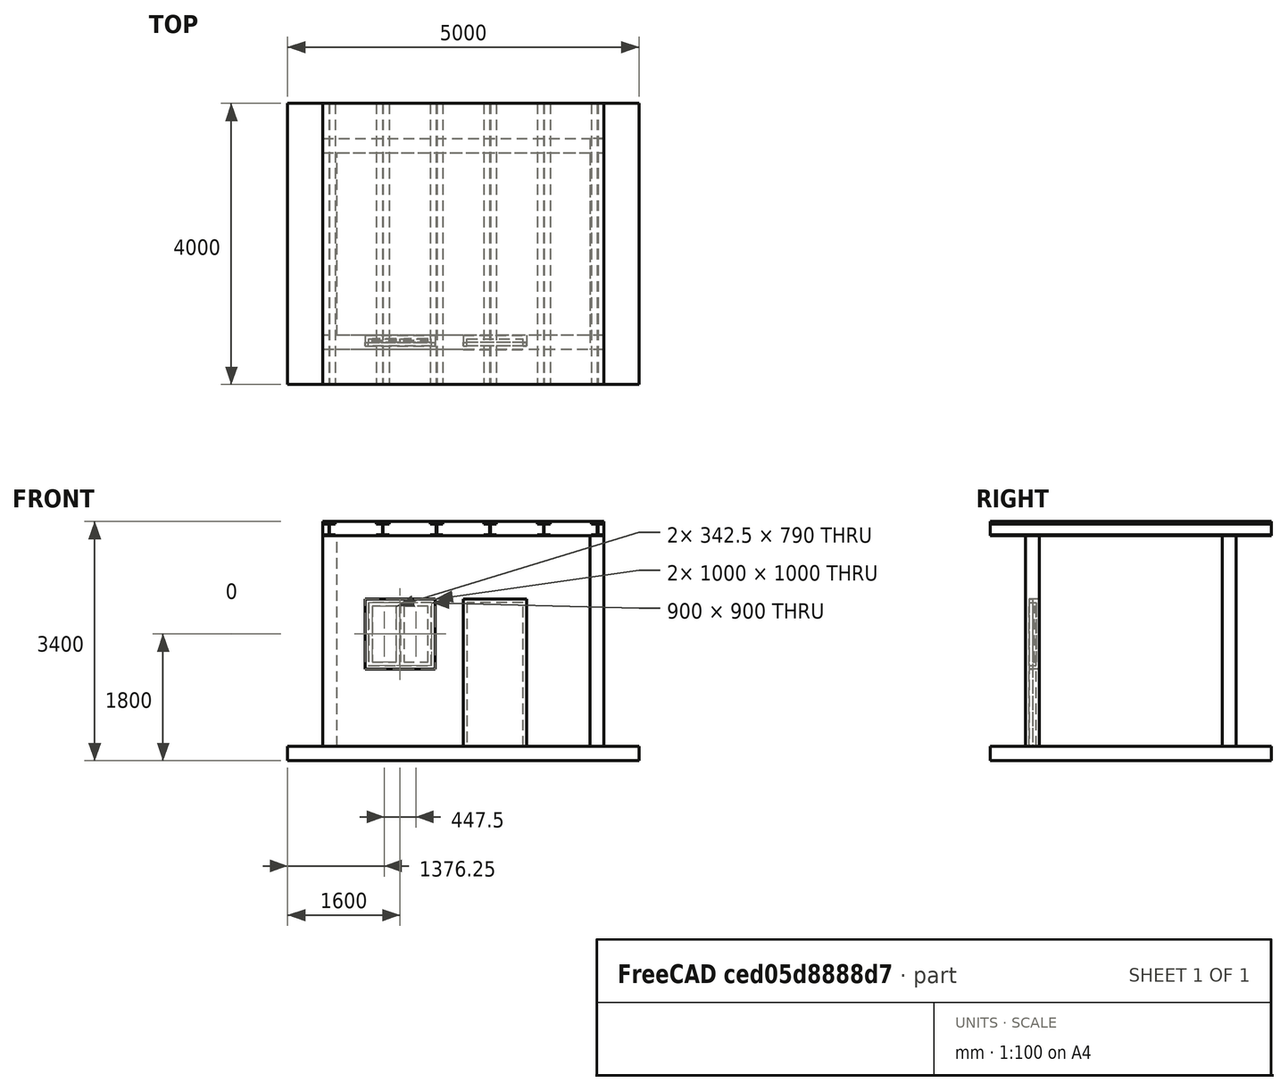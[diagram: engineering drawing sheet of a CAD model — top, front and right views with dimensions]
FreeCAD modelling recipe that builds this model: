
FCSTD DOCUMENT  (FreeCAD 0.17R7451 (Git))
Label: fem
License: All rights reserved
LicenseURL: http://en.wikipedia.org/wiki/All_rights_reserved
objects: Part::FeaturePython×12, Part::Part2DObjectPython×7, Sketcher::SketchObject×2, App::DocumentObjectGroupPython×2, Part::Feature×2, Part::MultiFuse×1, Fem::FemSolverObjectPython×1, Fem::FemMeshShapeNetgenObject×1, App::MaterialObjectPython×1, Fem::ConstraintFixed×1, Fem::ConstraintPressure×1, Fem::FemResultObject×1, Fem::FemAnalysisPython×1
note: 24 computed .brp shape members not serialized (recipe doc carries the construction recipe); baked Part::Feature solids carry a one-line shape summary decoded from their .brp

FEATURE [Part::Part2DObjectPython] Line  # Draft 2D object (typed FeaturePython)
  ChamferSize = 0
  Closed = false
  End = (0,3000,0)
  FilletRadius = 0
  Length = 3000
  MakeFace = false
  Points = (2) [(0,0,0),(0,3000,0)]
  Start = (0,0,0)
  Subdivisions = 0
FEATURE [Part::Part2DObjectPython] Line001  # Draft 2D object (typed FeaturePython)
  ChamferSize = 0
  Closed = false
  End = (4000,3000,0)
  FilletRadius = 0
  Length = 4000
  MakeFace = false
  Points = (2) [(0,3000,0),(4000,3000,0)]
  Start = (0,3000,0)
  Subdivisions = 0
FEATURE [Part::Part2DObjectPython] Line002  # Draft 2D object (typed FeaturePython)
  ChamferSize = 0
  Closed = false
  End = (4000,0,0)
  FilletRadius = 0
  Length = 3000
  MakeFace = false
  Points = (2) [(4000,3000,0),(4000,0,0)]
  Start = (4000,3000,0)
  Subdivisions = 0
FEATURE [Part::FeaturePython] Wall002  # WARN: FeaturePython — macro-defined, semantics opaque (R4)
  Align = 0
  Base = -> Line001
  Face = 0
  Height = 3000
  Length = 4000
  MoveWithHost = false
  Normal = (0,0,0)
  Role = 0
  Width = 200
FEATURE [Part::FeaturePython] Wall003  # WARN: FeaturePython — macro-defined, semantics opaque (R4)
  Align = 0
  Base = -> Line002
  Face = 0
  Height = 3000
  Length = 3000
  MoveWithHost = false
  Normal = (0,0,0)
  Role = 0
  Width = 200
FEATURE [Part::Part2DObjectPython] Line003  # Draft 2D object (typed FeaturePython)
  ChamferSize = 0
  Closed = false
  End = (0,0,0)
  FilletRadius = 0
  Length = 4000
  MakeFace = false
  Points = (2) [(4000,0,0),(0,0,0)]
  Start = (4000,0,0)
  Subdivisions = 0
FEATURE [Part::FeaturePython] Wall004  # WARN: FeaturePython — macro-defined, semantics opaque (R4)
  Align = 0
  Base = -> Line003
  Face = 0
  Height = 3000
  Length = 4000
  MoveWithHost = false
  Normal = (0,0,0)
  Role = 0
  Width = 200
FEATURE [Part::FeaturePython] Wall  # WARN: FeaturePython — macro-defined, semantics opaque (R4)
  Additions = -> [Wall004,Wall003,Wall002]
  Align = 0
  Base = -> Line
  Face = 0
  Height = 3000
  Length = 3000
  MoveWithHost = false
  Normal = (0,0,0)
  Role = 0
  Width = 200
FEATURE [Part::Part2DObjectPython] HEB180  # Draft 2D object (typed FeaturePython)
  FlangeThickness = 14
  Height = 180
  WebThickness = 8.5
  Width = 180
FEATURE [Part::FeaturePython] Structure  # WARN: FeaturePython — macro-defined, semantics opaque (R4)
  Base = -> HEB180
  Height = 4000
  Length = 0
  MoveWithHost = false
  Nodes = (2) [(1.65295e-14,-4.59631e-15,0),(1.65295e-14,-4.59631e-15,4000)]
  Normal = (0,0,0)
  Placement = pos=(90,3500,3090) rot=(1,0,0;1.5708rad)
  Profile = HEB180
  Role = 1
  Width = 200
FEATURE [Part::FeaturePython] Array  # Draft array (typed FeaturePython)
  Angle = 360
  ArrayType = 0
  Axis = (0,0,1)
  Base = -> Structure
  Center = (0,0,0)
  Fuse = false
  IntervalAxis = (0,0,0)
  IntervalX = (764,0,0)
  IntervalY = (0,1,0)
  IntervalZ = (0,0,0)
  NumberPolar = 1
  NumberX = 6
  NumberY = 1
  NumberZ = 1
FEATURE [Sketcher::SketchObject] Sketch
  MapMode = 5
  Placement = pos=(2000,0,0) rot=(1,0,0;1.5708rad)
  sketch-geometry (8):
    g0: LineSegment StartX=0 StartY=0 StartZ=0 EndX=900 EndY=0 EndZ=0
    g1: LineSegment StartX=900 StartY=0 StartZ=0 EndX=900 EndY=2100 EndZ=0
    g2: LineSegment StartX=900 StartY=2100 StartZ=0 EndX=0 EndY=2100 EndZ=0
    g3: LineSegment StartX=0 StartY=2100 StartZ=0 EndX=0 EndY=0 EndZ=0
    g4: LineSegment StartX=50 StartY=0 StartZ=0 EndX=850 EndY=0 EndZ=0
    g5: LineSegment StartX=850 StartY=0 StartZ=0 EndX=850 EndY=2050 EndZ=0
    g6: LineSegment StartX=850 StartY=2050 StartZ=0 EndX=50 EndY=2050 EndZ=0
    g7: LineSegment StartX=50 StartY=2050 StartZ=0 EndX=50 EndY=0 EndZ=0
  constraints (23):
    c: Coincident(g0,g1)
    c: Coincident(g1,g2)
    c: Coincident(g2,g3)
    c: Coincident(g3,g0)
    c: Horizontal(g0)
    c: Horizontal(g2)
    c: Vertical(g1)
    c: Vertical(g3)
    c: Coincident(g4,g5)
    c: Coincident(g5,g6)
    c: Coincident(g6,g7)
    c: Coincident(g7,g4)
    c: Horizontal(g4)
    c: Horizontal(g6)
    c: Vertical(g5)
    c: Vertical(g7)
    c: DistanceY(g1) = 2100
    c: DistanceX(g0) = 900
    c: DistanceY(g6,g2) = 50
    c: DistanceX(g2,g6) = 50
    c: DistanceX(g4,g0) = 50
    c: DistanceY(g0,g4) = 0
    c: Coincident(g0,g-1)
FEATURE [Part::FeaturePython] Window  # WARN: FeaturePython — macro-defined, semantics opaque (R4)
  Base = -> Sketch
  Height = 2100
  HoleDepth = 0
  MoveWithHost = true
  Normal = (0,1,0)
  Preset = 6
  Role = 1
  Width = 900
  WindowParts = OuterFrame | Frame | Wire0,Wire1 | 50.0 | 50.0 | Door | Solid panel | Wire1 | 50.0 | 100.0
FEATURE [Part::FeaturePython] Wall005  # WARN: FeaturePython — macro-defined, semantics opaque (R4)
  Align = 2
  Base = -> Wall
  Face = 0
  Height = 2000
  Length = 0
  MoveWithHost = false
  Normal = (0,0,0)
  Role = 0
  Subtractions = -> [Window]
  Width = 200
FEATURE [Sketcher::SketchObject] Sketch001
  MapMode = 5
  Placement = pos=(600,0,1100) rot=(1,0,0;1.5708rad)
  sketch-geometry (24):
    g0: LineSegment StartX=0 StartY=0 StartZ=0 EndX=1000 EndY=0 EndZ=0
    g1: LineSegment StartX=1000 StartY=0 StartZ=0 EndX=1000 EndY=1000 EndZ=0
    g2: LineSegment StartX=1000 StartY=1000 StartZ=0 EndX=0 EndY=1000 EndZ=0
    g3: LineSegment StartX=0 StartY=1000 StartZ=0 EndX=0 EndY=0 EndZ=0
    g4: LineSegment StartX=50 StartY=50 StartZ=0 EndX=950 EndY=50 EndZ=0
    g5: LineSegment StartX=950 StartY=50 StartZ=0 EndX=950 EndY=950 EndZ=0
    g6: LineSegment StartX=950 StartY=950 StartZ=0 EndX=50 EndY=950 EndZ=0
    g7: LineSegment StartX=50 StartY=950 StartZ=0 EndX=50 EndY=50 EndZ=0
    g8: LineSegment StartX=55 StartY=55 StartZ=0 EndX=497.5 EndY=55 EndZ=0
    g9: LineSegment StartX=497.5 StartY=55 StartZ=0 EndX=497.5 EndY=945 EndZ=0
    g10: LineSegment StartX=497.5 StartY=945 StartZ=0 EndX=55 EndY=945 EndZ=0
    g11: LineSegment StartX=55 StartY=945 StartZ=0 EndX=55 EndY=55 EndZ=0
    g12: LineSegment StartX=105 StartY=105 StartZ=0 EndX=447.5 EndY=105 EndZ=0
    g13: LineSegment StartX=447.5 StartY=105 StartZ=0 EndX=447.5 EndY=895 EndZ=0
    g14: LineSegment StartX=447.5 StartY=895 StartZ=0 EndX=105 EndY=895 EndZ=0
    g15: LineSegment StartX=105 StartY=895 StartZ=0 EndX=105 EndY=105 EndZ=0
    g16: LineSegment StartX=502.5 StartY=55 StartZ=0 EndX=945 EndY=55 EndZ=0
    g17: LineSegment StartX=945 StartY=55 StartZ=0 EndX=945 EndY=945 EndZ=0
    g18: LineSegment StartX=945 StartY=945 StartZ=0 EndX=502.5 EndY=945 EndZ=0
    g19: LineSegment StartX=502.5 StartY=945 StartZ=0 EndX=502.5 EndY=55 EndZ=0
    g20: LineSegment StartX=552.5 StartY=105 StartZ=0 EndX=895 EndY=105 EndZ=0
    g21: LineSegment StartX=895 StartY=105 StartZ=0 EndX=895 EndY=895 EndZ=0
    g22: LineSegment StartX=895 StartY=895 StartZ=0 EndX=552.5 EndY=895 EndZ=0
    g23: LineSegment StartX=552.5 StartY=895 StartZ=0 EndX=552.5 EndY=105 EndZ=0
  constraints (71):
    c: Coincident(g0,g1)
    c: Coincident(g1,g2)
    c: Coincident(g2,g3)
    c: Coincident(g3,g0)
    c: Horizontal(g0)
    c: Horizontal(g2)
    c: Vertical(g1)
    c: Vertical(g3)
    c: Coincident(g4,g5)
    c: Coincident(g5,g6)
    c: Coincident(g6,g7)
    c: Coincident(g7,g4)
    c: Horizontal(g4)
    c: Horizontal(g6)
    c: Vertical(g5)
    c: Vertical(g7)
    c: DistanceY(g1) = 1000
    c: DistanceX(g0) = 1000
    c: DistanceY(g6,g2) = 50
    c: DistanceX(g2,g6) = 50
    c: DistanceX(g4,g0) = 50
    c: DistanceY(g0,g4) = 50
    c: Coincident(g0,g-1)
    c: Coincident(g8,g9)
    c: Coincident(g9,g10)
    c: Coincident(g10,g11)
    c: Coincident(g11,g8)
    c: Horizontal(g8)
    c: Horizontal(g10)
    c: Vertical(g9)
    c: Vertical(g11)
    c: Coincident(g12,g13)
    c: Coincident(g13,g14)
    c: Coincident(g14,g15)
    c: Coincident(g15,g12)
    c: Horizontal(g12)
    c: Horizontal(g14)
    c: Vertical(g13)
    c: Vertical(g15)
    c: Coincident(g16,g17)
    c: Coincident(g17,g18)
    c: Coincident(g18,g19)
    c: Coincident(g19,g16)
    c: Horizontal(g16)
    c: Horizontal(g18)
    c: Vertical(g17)
    c: Vertical(g19)
    c: Coincident(g20,g21)
    c: Coincident(g21,g22)
    c: Coincident(g22,g23)
    c: Coincident(g23,g20)
    c: Horizontal(g20)
    c: Horizontal(g22)
    c: Vertical(g21)
    c: Vertical(g23)
    c: DistanceY(g8,g12) = 50
    c: DistanceX(g8,g12) = 50
    c: DistanceX(g21,g17) = 50
    c: DistanceY(g21,g17) = 50
    c: DistanceX(g16,g20) = 50
    c: DistanceX(g14,g10) = 50
    c: Equal(g22,g14)
    c: DistanceY(g8,g16) = 0
    c: DistanceY(g10,g18) = 0
    c: DistanceX(g4,g8) = 5
    c: DistanceY(g4,g8) = 5
    c: DistanceX(g6,g18) = -5
    c: DistanceY(g6,g18) = -5
    c: DistanceX(g9,g19) = 5
    c: PointOnObject(g13,g22)
    c: PointOnObject(g20,g12)
FEATURE [Part::FeaturePython] Window001  # WARN: FeaturePython — macro-defined, semantics opaque (R4)
  Base = -> Sketch001
  Height = 1000
  HoleDepth = 0
  MoveWithHost = true
  Normal = (0,1,0)
  Preset = 3
  Role = 0
  Width = 1000
  WindowParts = OuterFrame | Frame | Wire0,Wire1 | 50.0 | 50.0 | LeftFrame | Frame | Wire2,Wire3 | 50.0 | 100.0 | LeftGlass | Glass panel | Wire3 | 5.0 | 125.0 | RightFrame | Frame | Wire4,Wire5 | 50.0 | 100.0 | RightGlass | Glass panel | Wire5 | 5.0 | 125.0
FEATURE [Part::FeaturePython] Wall006  # WARN: FeaturePython — macro-defined, semantics opaque (R4)
  Align = 2
  Base = -> Wall005
  Face = 0
  Height = 2000
  Length = 0
  MoveWithHost = false
  Normal = (0,0,0)
  Role = 0
  Subtractions = -> [Window001]
  Width = 200
FEATURE [Part::Part2DObjectPython] Rectangle  # Draft 2D object (typed FeaturePython)
  ChamferSize = 0
  Columns = 1
  FilletRadius = 0
  Height = -4000
  Length = -4000
  MakeFace = true
  Placement = pos=(0,-500,3000) rot=(0,0,1;3.14159rad)
  Rows = 1
FEATURE [Part::FeaturePython] Structure001  # WARN: FeaturePython — macro-defined, semantics opaque (R4)
  Base = -> Rectangle
  Height = 200
  Length = 0
  MoveWithHost = false
  Nodes = (2) [(2000,1500,3000),(2000,1500,3200)]
  Normal = (0,0,1)
  Role = 1
  Width = 200
FEATURE [Part::Part2DObjectPython] Rectangle001  # Draft 2D object (typed FeaturePython)
  ChamferSize = 0
  Columns = 1
  FilletRadius = 0
  Height = -4000
  Length = 5000
  MakeFace = true
  Placement = pos=(-500,3500,0) rot=(0,0,1;0rad)
  Rows = 1
FEATURE [Part::FeaturePython] Structure002  # WARN: FeaturePython — macro-defined, semantics opaque (R4)
  Base = -> Rectangle001
  Height = 200
  Length = 0
  MoveWithHost = false
  Nodes = (2) [(2000,1500,0),(2000,1500,-200)]
  Normal = (0,0,-1)
  Role = 1
  Width = 200
FEATURE [App::DocumentObjectGroupPython] Floor  # scripted group (container) (typed FeaturePython)
  Group = -> [Array,Wall006,Structure001,Structure002]
  Height = 0
FEATURE [App::DocumentObjectGroupPython] Building  # scripted group (container) (typed FeaturePython)
  BuildingType = 0
  Group = -> [Floor]
  Height = 0
FEATURE [Part::Feature] Wall006001  label="Wall007"
  shape: bbox 4000 x 3000 x 3000 mm, 17 faces (baked)
FEATURE [Part::Feature] Structure001001  label="Structure003"
  shape: bbox 4000 x 4000 x 200 mm, 6 faces (baked)
FEATURE [Part::MultiFuse] Fusion
  Shapes = -> [Wall006001,Structure001001]
FEATURE [Fem::FemSolverObjectPython] CalculiX  # FEM object (typed FeaturePython)
  AnalysisType = 0
  EigenmodeHighLimit = 1000000
  EigenmodeLowLimit = 0
  NumberOfEigenmodes = 10
  SolverType = FemSolverCalculix
FEATURE [Fem::FemMeshShapeNetgenObject] Fusion_Mesh
  Fineness = 2
  GrowthRate = 0.3
  MaxSize = 1000
  NbSegsPerEdge = 1
  NbSegsPerRadius = 2
  Optimize = true
  SecondOrder = true
  Shape = -> Fusion
FEATURE [App::MaterialObjectPython] MechanicalMaterial  # material (typed FeaturePython)
  Material = CompressiveStrength=25 MPa,Density=2400 kg/m^3,Description=A standard C-25 construction concrete,Father=Aggregate,Name=Concrete,PoissonRatio=0.17,+3 more (map truncated)
FEATURE [Fem::ConstraintFixed] FemConstraintFixed
  NormalDirection = (0,0,-1)
  Normals = (24) [(0,0,-1),(0,0,-1),(0,0,-1),(0,0,-1),(0,0,-1),(0,0,-1),(0,0,-1),(0,0,-1),(0,0,-1),(0,0,-1),(0,0,-1),(0,0,-1),(0,0,-1),(0,0,-1),(0,0,-1),(0,0,-1),+8 more]
  Points = (24) [(0,0,0),(571.429,0,0),(1142.86,0,0),(1714.29,0,0),(3428.57,0,0),(4000,0,0),(0,500,0),(4000,500,0),(0,1000,0),(4000,1000,0),(0,1500,0),(4000,1500,0),+12 more]
  References = -> [Fusion]
  Scale = 54
FEATURE [Fem::ConstraintPressure] FemConstraintPressure
  NormalDirection = (0,0,1)
  Normals = (64) [(0,0,1),(0,0,1),(0,0,1),(0,0,1),(0,0,1),(0,0,1),(0,0,1),(0,0,1),(0,0,1),(0,0,1),(0,0,1),(0,0,1),(0,0,1),(0,0,1),(0,0,1),(0,0,1),(0,0,1),(0,0,1),+46 more]
  Points = (64) [(4.89859e-13,3500,3200),(571.429,3500,3200),(1142.86,3500,3200),(1714.29,3500,3200),(2285.71,3500,3200),(2857.14,3500,3200),(3428.57,3500,3200),+57 more]
  Pressure = 10
  References = -> [Fusion]
  Scale = 57
FEATURE [Fem::FemResultObject] Results
  DisplacementLengths = [4.56124,4.40504,6.8588,6.06264,2.1132,9.1358,8.22723,22.5634,23.7244,14.6082,0,0,0,0,0,0,2.59093,10.9347,9.50838,22.4229,0,23.5827,15.6984,0,0,0,0,0,5.45753,3.36362,5.28805,4.45724,5.10115,3.48167,5.56485,5.63871,7.10488,6.8253,8.06963,+9740 more]
  DisplacementVectors = (9779) [(-0.415784,-0.756211,-4.47886),(-0.300936,-1.11885,-4.24994),(-0.349177,-1.46601,-6.69119),(-0.879952,-1.70441,-5.7512),(-1.33743,-1.15249,-1.16132),+9774 more]
  Eigenmode = 0
  EigenmodeFrequency = 0
  Mesh = -> Fusion_Mesh
  NodeNumbers = [1,2,3,4,5,6,7,8,9,10,11,12,13,14,15,16,17,18,19,20,21,22,23,24,25,26,27,28,29,30,31,32,33,34,35,36,37,38,39,40,41,42,43,44,45,46,47,48,49,50,51,52,53,54,55,56,57,58,59,60,61,62,63,64,65,66,67,68,69,+9710 more]
  Stats = [-12.9289,-0.324633,11.6418,-20.6607,-1.11361,13.981,-87.2757,-8.32123,7.9723,0,10.127,87.2839,5.01952,108.458,461.342]
  StressValues = [58.1868,68.0135,78.9785,68.1374,117.609,336.565,246.824,260.881,321.075,324.5,36.296,56.9074,44.7007,43.765,75.9969,20.6343,87.7679,246.766,312.747,147.007,154.363,188.24,179.573,39.9511,78.7575,165.148,98.1079,97.5735,14.5754,87.2655,+9749 more]
FEATURE [Fem::FemAnalysisPython] MechanicalAnalysis  # FEM object (typed FeaturePython)
  Member = -> [CalculiX,Fusion_Mesh,MechanicalMaterial,FemConstraintFixed,FemConstraintPressure,Results]
